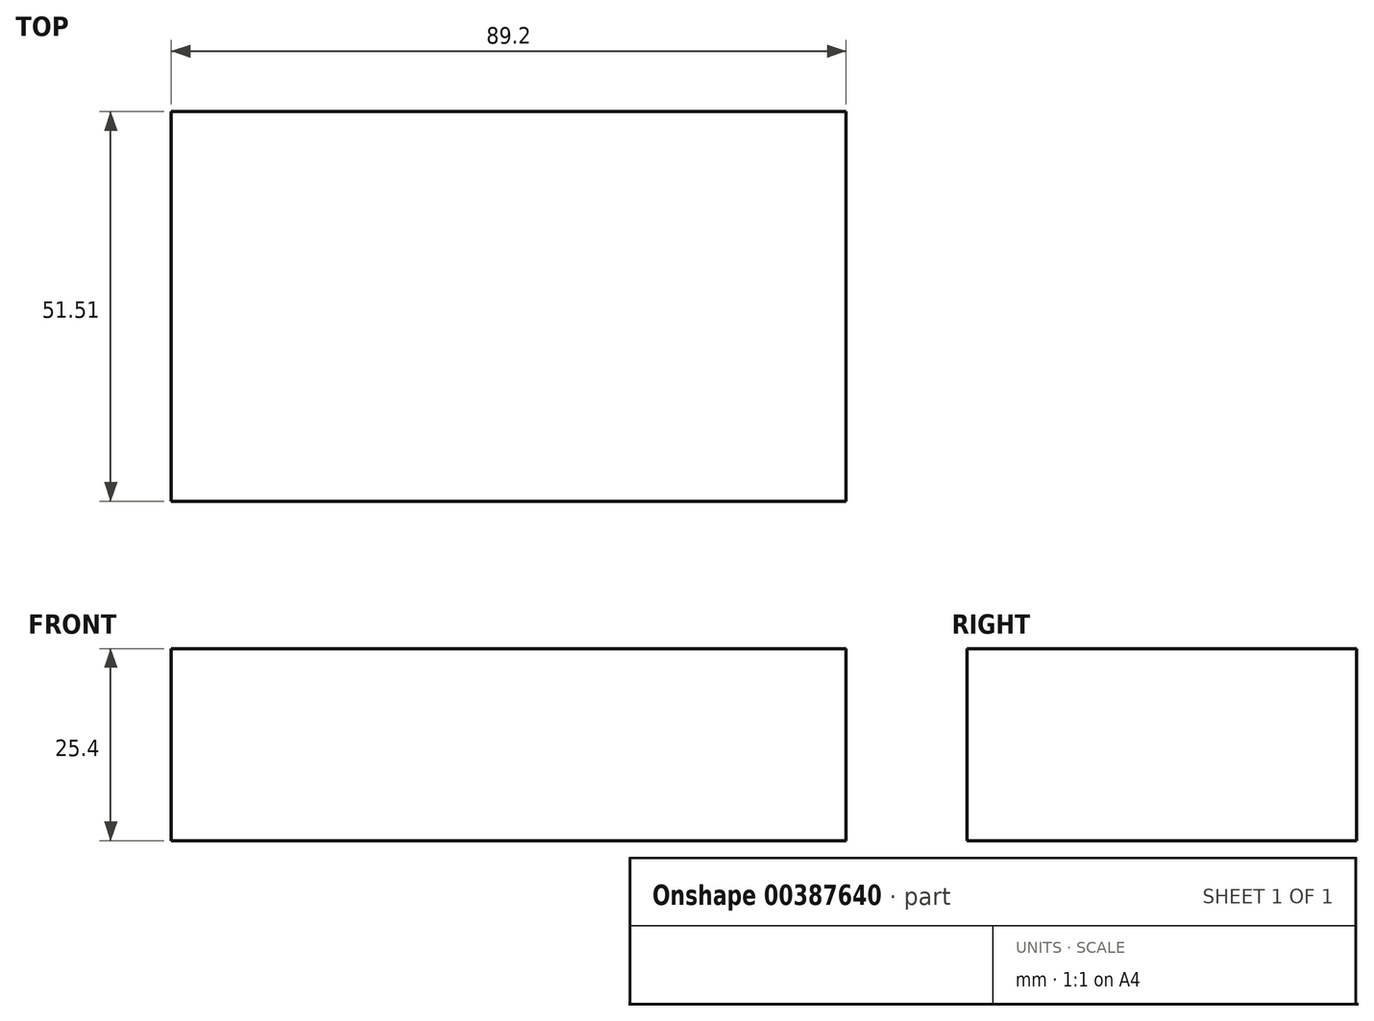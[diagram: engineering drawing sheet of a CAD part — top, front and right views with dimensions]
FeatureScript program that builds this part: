
annotation { "Feature Type Name" : "Feature", "Feature Type Description" : "" }
export const myFeature = defineFeature(function(context is Context, id is Id, definition is map)
    precondition{}
    {
        {
            var Q0;
            Q0=qCreatedBy(makeId("Top.planeOp"),FACE);
            var sketch = newSketch(context, id + "F0", { "sketchPlane" : qUnion([Q0])});
            skLineSegment(sketch, "E0", {"start": v(-62.08, 69.17) * mm, "end": v(80.17, 29.33) * mm});
            skLineSegment(sketch, "E1", {"start": v(80.17, 29.33) * mm, "end": v(80.9, -33.97) * mm});
            skLineSegment(sketch, "E2", {"start": v(80.9, -33.97) * mm, "end": v(-56.7, -60.13) * mm});
            skLineSegment(sketch, "E3.bottom", {"start": v(71, -26.76) * mm, "end": v(-18.2, -26.76) * mm});
            skLineSegment(sketch, "E3.top", {"start": v(71, 24.75) * mm, "end": v(-18.2, 24.75) * mm});
            skLineSegment(sketch, "E3.left", {"start": v(71, -26.76) * mm, "end": v(71, 24.75) * mm});
            skLineSegment(sketch, "E3.right", {"start": v(-18.2, -26.76) * mm, "end": v(-18.2, 24.75) * mm});
            skLineSegment(sketch, "E4.bottom", {"start": v(59.09, -15.56) * mm, "end": v(-18.2, -15.56) * mm});
            skLineSegment(sketch, "E4.top", {"start": v(59.09, 11.6) * mm, "end": v(-18.2, 11.6) * mm});
            skLineSegment(sketch, "E4.left", {"start": v(59.09, -15.56) * mm, "end": v(59.09, 11.6) * mm});
            skLineSegment(sketch, "E4.right", {"start": v(-18.2, -15.56) * mm, "end": v(-18.2, 11.6) * mm});
            skSolve(sketch);
        }
        {
            var Q0;
            Q0=makeQuery(id+"F0.imprint","IMPRINT",FACE,{"disambiguationData":[TD([[makeQuery(id+"F0.imprint","IMPRINT",EDGE,{"derivedFrom":sQuery(id+"F0.wireOp",EDGE,"E4.bottom")}),-1.0]])]});
            var Q1;
            {var subQ1=sQuery(id+"F0.wireOp",EDGE,"E3.bottom");Q1=makeQuery(id+"F0.imprint","IMPRINT",FACE,{"disambiguationData":[TD([[makeQuery(id+"F0.imprint","IMPRINT",EDGE,{"derivedFrom":subQ1}),-1.0]])]});}
            extrude(context, id + "F1", {"entities" : qUnion([Q0, Q1]), "depth" : 25.4 * mm});
        }
    });
